# Revit family: Gira_018100
name_source: partatom
category: Allgemeines Modell
revit_build: Autodesk Revit 2017 (Build: 20160225_1515(x64)
units: mm (PartAtom-declared; Revit-internal decimal feet)

## family parameters
Basisbauteil = Fläche
Beim Laden mit Abzugskörper schneiden = Nein
Bemaßung runder Anschluss = Durchmesser verwenden
Gemeinsam genutzt = Nein
Kann Basisbauteil für Bewehrung sein = Nein
Raumberechnungspunkt = Nein
Teiletyp = Normal

## types (1)
- Gira_018100
    App control via Bluetooth = Nein
    Applicable with button = Ja
    Applicable with infrared button = Nein
    Applicable with movement sensor = Ja
    Applicable with presence indicator = Ja
    Applicable with time switch/timer = Nein
    Applicable with transmission button = Nein
    Assembly arrangement = Basic element
    BIM = https://media.stage.bim.site
    Beschreibung = Ins.b.cpl.btn 1g 1-pt LED KNX,Insert for KNX bus coupler button, 1-gang with single-point operation and status LED,,,The bus coupler button is the interface between the KNX system and the user.,,Features:,- The 1-gang rockers of the flush-mounted design lines can be inserted on the bus coupler button, 1-gang with single-point operation (slanted rocker).,- When using the status LED, please use rockers with control window.,- The switching (pressing) functions can be realised with the bus coupler button, 1-gang with single-point operation.,- LED display for: permanent-on or permanent-off or status.,,Notes :,- Suitable for claw mounting.,- Please use System 55 adapter frame and cover for Gira TX_44 design line, IP20.,- Integration in the Gira F100 design line is not possible.,- Integration in Gira F100 not possible.
    Bus connection included = Ja
    Bus system KNX = Ja
    Bus system KNX radio = Nein
    Bus system LON = Nein
    Bus system Powernet = Nein
    Bus system radio frequent = Nein
    Category = 5
    Colour = Other
    Colour coding = Nein
    Connection type = Screw
    Data sheet = https://katalog.gira.de
    Degree of protection (IP) = IP20
    Dimming phase cut-off = Ja
    Dimming phase cut-on = Ja
    Electrical and mechanical locking = Ja
    Electronic controllable = Nein
    Forced switch off = Nein
    Frequency [Hz] = [50:60]
    Function lighting = Illuminated (on)
    GTIN = 4010337181002
    HAN = 018100
    Halogen free = Nein
    Hersteller = Gira
    Illumination = Yes
    Imprint = None
    Input for substation = Nein
    Integrated timer = Nein
    Label space/information surface = Nein
    Label space/information surface 4 = No
    Label space/information surface 5 = No
    Label space/information surface 6 = No
    Label space/information surface 7 = No
    Light value memory = Nein
    Material = Other
    Material quality = Other
    Max. output current = 1 A
    Max. switching power [Voltampere] = 1000
    Mechanical coding = Nein
    Mechanical controllable = Ja
    Method of operation = Rocker
    Min. depth of built-in installation box [m] = 0.024
    Model = 1-pole switch
    Mounting method = Flush mounted (plaster)
    Mounting method shielding connection = None
    Nominal voltage [Volt] = 250
    Nominal voltage [Volt] 2 = [230:230]
    Nominal voltage [Volt] 3 = [230:230]
    Number of buttons = 2
    Number of modules (module system) = 1
    Number of outputs = 2
    Number of rockers = 1
    Only suitable as substation = Nein
    Operating voltage [Volt] = [110:240]
    Other bus systems = None
    Output voltage [Volt] = 5
    Productwebsite = http://katalog.gira.de
    Push button switch = Nein
    Random generator = Nein
    Rated current = 10 A
    Separate strain relief = Ja
    Serial dimmer = Nein
    Shielded buses = Ja
    Shielded housing = Nein
    Substation input = Ja
    Suitable for 230 V incandescent lamp/halogen lamp = Ja
    Suitable for degree of protection (IP) = IP20
    Suitable for electronic low voltage transformer = Ja
    Suitable for fluorescent tube/energy-saving lamp = Ja
    Suitable for rain sensor = Nein
    Suitable for staircase time switch = Nein
    Suitable for wind sensor = Nein
    Suitable for wire wound low voltage transformer = Ja
    Surface finishing = Not applicable
    Surface protection = Other
    Switch-off protection = Nein
    Temperature [Kelvin] = [5:45]
    Through loss at 2150 MHz [B] = 0.1
    Through loss at 860 MHz [B] = 0.1
    Transparent = Nein
    Type of fastening = Mounting with claw and screw
    Type of lighting = Not included
    Type of load = Universal
    Typname = Bus coup.btn 1-g 1-point + status LED KNX insert
    URL = https://www.gira.de
    Vorgabe-Ansicht = 1219 mm
    Washing machine switch = Nein
    Wiring system = Intermediate switch
    With Astro program = Nein
    With LED indication = Nein
    With N-busbar = Nein
    With brightness sensor connection = Nein
    With dust cover = Nein
    With glass breaking detector connection = Nein
    With label area = Nein
    With lighting = Nein
    With memory function = Nein
    With mounting plate = Nein

## geometry (parser evidence)
native form markers: Sweep x2
no freeform markers — native parametric forms only
